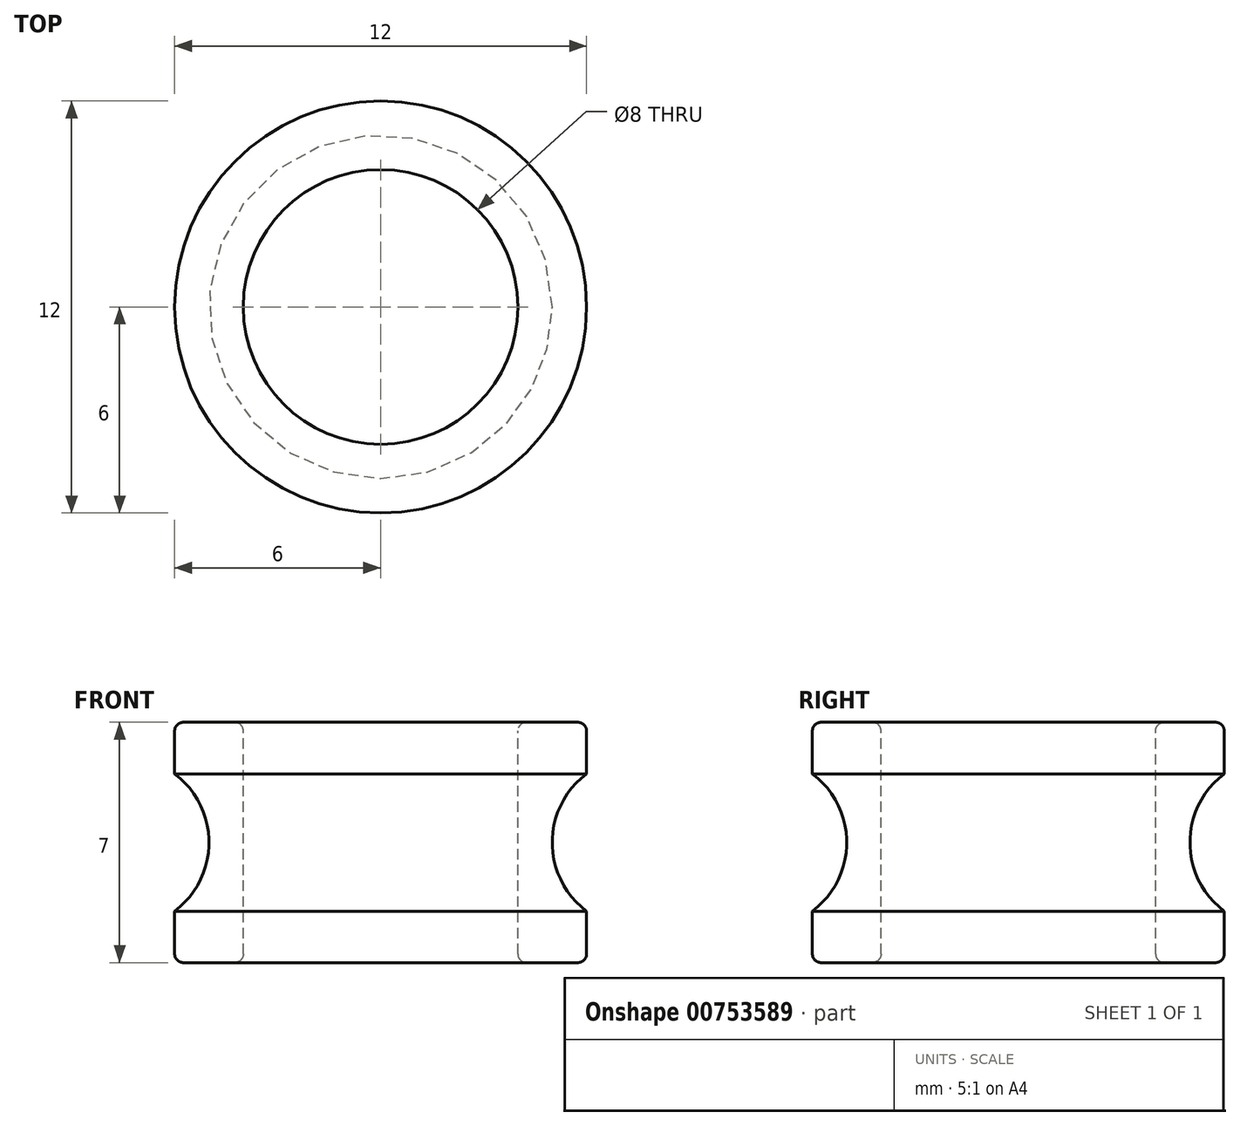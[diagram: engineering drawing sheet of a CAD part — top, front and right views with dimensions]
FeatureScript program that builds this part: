
annotation { "Feature Type Name" : "Feature", "Feature Type Description" : "" }
export const myFeature = defineFeature(function(context is Context, id is Id, definition is map)
    precondition{}
    {
        {
            var Q0;
            Q0=qCreatedBy(makeId("Front.planeOp"),FACE);
            var sketch = newSketch(context, id + "F0", { "sketchPlane" : qUnion([Q0])});
            skLineSegment(sketch, "E0", {"start": v(0, 4.7) * mm, "end": v(0, -4.02) * mm});
            skLineSegment(sketch, "E1", {"start": v(4, 0) * mm, "end": v(6, 0) * mm});
            skLineSegment(sketch, "E2", {"start": v(4, 0) * mm, "end": v(4, 3.25) * mm});
            skLineSegment(sketch, "E3", {"start": v(4, 0) * mm, "end": v(4, -3.25) * mm});
            skLineSegment(sketch, "E4", {"start": v(0, 0) * mm, "end": v(4, 0) * mm});
            skLineSegment(sketch, "E5", {"start": v(4.25, 3.5) * mm, "end": v(5.75, 3.5) * mm});
            skLineSegment(sketch, "E6", {"start": v(4.25, -3.5) * mm, "end": v(5.75, -3.5) * mm});
            skLineSegment(sketch, "E7", {"start": v(6, -3.25) * mm, "end": v(6, -2) * mm});
            skArc(sketch, "E8", {"start": v(6, 2) * mm, "mid": v(5, 0) * mm, "end": v(6, -2) * mm});
            skPoint(sketch, "E9.end.orphan", {"position": v(11, -3.5) * mm});
            skPoint(sketch, "E10.start.orphan", {"position": v(11, 3.5) * mm});
            skPoint(sketch, "E11.start.orphan", {"position": v(9, 3.5) * mm});
            skPoint(sketch, "E12.trimOffspring.end.orphan", {"position": v(9, -3.5) * mm});
            skPoint(sketch, "E13.trimOffspring.end.orphan", {"position": v(11, 0) * mm});
            skLineSegment(sketch, "E14.trimOffspring", {"start": v(6, 2) * mm, "end": v(6, 3.25) * mm});
            skPoint(sketch, "E15.visualSharp", {"position": v(4, 3.5) * mm});
            skArc(sketch, "E15.filletArc", {"start": v(4.25, 3.5) * mm, "mid": v(4.07, 3.43) * mm, "end": v(4, 3.25) * mm});
            skPoint(sketch, "E16.visualSharp", {"position": v(4, -3.5) * mm});
            skArc(sketch, "E16.filletArc", {"start": v(4, -3.25) * mm, "mid": v(4.07, -3.43) * mm, "end": v(4.25, -3.5) * mm});
            skPoint(sketch, "E17.visualSharp", {"position": v(6, -3.5) * mm});
            skArc(sketch, "E17.filletArc", {"start": v(5.75, -3.5) * mm, "mid": v(5.93, -3.43) * mm, "end": v(6, -3.25) * mm});
            skPoint(sketch, "E18.visualSharp", {"position": v(6, 3.5) * mm});
            skArc(sketch, "E18.filletArc", {"start": v(6, 3.25) * mm, "mid": v(5.93, 3.43) * mm, "end": v(5.75, 3.5) * mm});
            skSolve(sketch);
        }
        {
            var Q0;
            Q0 = qSketchRegion(id + "F0", true);
            var Q1;
            Q1=sQuery(id+"F0.wireOp",EDGE,"E0");
            revolve(context, id + "F1", {"surfaceOperationType" : NewSurfaceOperationType.NEW, "entities" : qUnion([Q0]), "axis" : qUnion([Q1]), "revolveType" : RevolveType.FULL});
        }
    });
